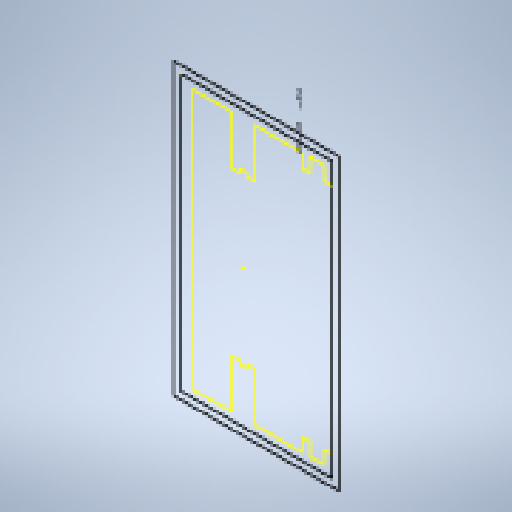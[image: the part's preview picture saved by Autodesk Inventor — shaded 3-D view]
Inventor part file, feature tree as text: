
AUTODESK INVENTOR PART (.ipt)
format: ipt  version: 2023 (Build 270158000, 158)  size: 173,568 bytes
history: native  units: mm
features: extrude x3, sketch x3, other x3, projected_geometry x1
ambient origin geometry x8: Origin, YZ Plane, XZ Plane, XY Plane, X Axis, Y Axis, Z Axis, Center Point
bodies: Solide1 (feature_tree)
feature tree (10):
  extrude  "Extrusion1"  Depth=2.0mm
  extrude  "Extrusion2"  Depth=2.0mm TaperAngle=0.0deg
  extrude  "Extrusion3"  Depth=2.0mm TaperAngle=0.0deg
  sketch  "Esquisse1"
  other  "Référence1"
  sketch  "Esquisse2"
  projected_geometry  "Boucle projetée1"
  sketch  "Esquisse3"
  other  "Ensemble2"
  other  "Remote:1"
